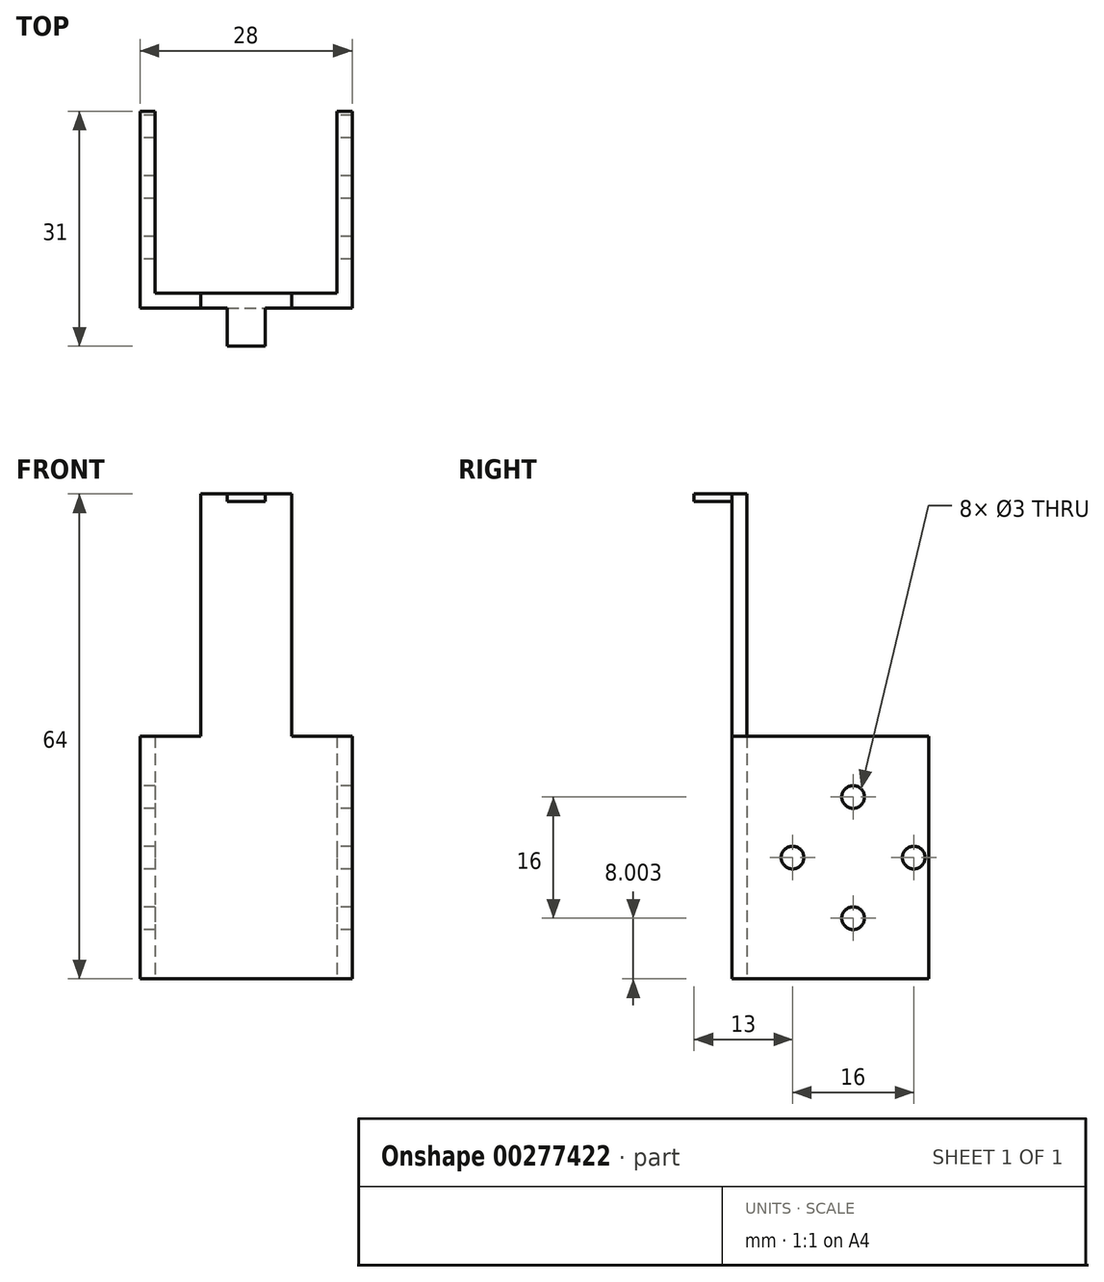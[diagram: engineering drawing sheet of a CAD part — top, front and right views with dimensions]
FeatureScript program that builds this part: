
annotation { "Feature Type Name" : "Feature", "Feature Type Description" : "" }
export const myFeature = defineFeature(function(context is Context, id is Id, definition is map)
    precondition{}
    {
        {
            var Q0;
            Q0=qCreatedBy(makeId("Front.planeOp"),FACE);
            var sketch = newSketch(context, id + "F0", { "sketchPlane" : qUnion([Q0])});
            skLineSegment(sketch, "E0.bottom", {"start": v(-7.9, 38.8) * mm, "end": v(4.1, 38.8) * mm});
            skLineSegment(sketch, "E0.top", {"start": v(-7.9, -25.2) * mm, "end": v(4.1, -25.2) * mm});
            skLineSegment(sketch, "E0.left", {"start": v(-7.9, 38.8) * mm, "end": v(-7.9, -25.2) * mm});
            skLineSegment(sketch, "E0.right", {"start": v(4.1, 38.8) * mm, "end": v(4.1, -25.2) * mm});
            skSolve(sketch);
        }
        {
            var Q0;
            Q0 = qSketchRegion(id + "F0", true);
            extrude(context, id + "F1", {"entities" : qUnion([Q0]), "depth" : 2 * mm});
        }
        {
            var Q0;
            Q0=makeQuery(id+"F1.opExtrude","SWEPT_FACE",FACE,{"disambiguationData":[OSD([sQuery(id+"F0.wireOp",EDGE,"E0.right")])]});
            var sketch = newSketch(context, id + "F2", { "sketchPlane" : qUnion([Q0])});
            skLineSegment(sketch, "E1", {"start": v(-2, 6.8) * mm, "end": v(0, 6.8) * mm});
            skSolve(sketch);
        }
        {
            var Q0;
            Q0 = qSketchRegion(id + "F2", true);
            var Q1;
            {var subQ0=sQuery(id+"F2.wireOp",EDGE,"E1");Q1=makeQuery(id+"F2.imprint","IMPRINT",FACE,{"disambiguationData":[TD([[makeQuery(id+"F2.imprint","IMPRINT",EDGE,{"derivedFrom":subQ0}),-1.0]])]});}
            extrude(context, id + "F3", {"entities" : qUnion([Q0, Q1]), "operationType" : NewBodyOperationType.ADD, "depth" : 8 * mm});
        }
        {
            var Q0;
            Q0=makeQuery(id+"F1.opExtrude","SWEPT_FACE",FACE,{"disambiguationData":[OSD([sQuery(id+"F0.wireOp",EDGE,"E0.left")])]});
            var sketch = newSketch(context, id + "F4", { "sketchPlane" : qUnion([Q0])});
            skLineSegment(sketch, "E2", {"start": v(2, 6.8) * mm, "end": v(0, 6.8) * mm});
            skSolve(sketch);
        }
        {
            var Q0;
            {var subQ0=sQuery(id+"F4.wireOp",EDGE,"E2");Q0=makeQuery(id+"F4.imprint","IMPRINT",FACE,{"disambiguationData":[TD([[makeQuery(id+"F4.imprint","IMPRINT",EDGE,{"derivedFrom":subQ0}),1.0]])]});}
            extrude(context, id + "F5", {"entities" : qUnion([Q0]), "operationType" : NewBodyOperationType.ADD, "depth" : 8 * mm});
        }
        {
            var Q0;
            {var subQ0=sQuery(id+"F0.wireOp",EDGE,"E0.left");var subQ1=makeQuery(id+"F1.opExtrude","CAP_EDGE",EDGE,{"disambiguationData":[OSD([subQ0])],"isStart":false});var subQ2=sQuery(id+"F0.wireOp",EDGE,"E0.top");var subQ3=sQuery(id+"F0.wireOp",EDGE,"E0.right");var subQ4=makeQuery(id+"F1.opExtrude","CAP_EDGE",EDGE,{"disambiguationData":[OSD([subQ3])],"isStart":false});Q0=makeQuery(id+"F5.boolean.opBoolean","MERGE",FACE,{"derivedFrom":[makeQuery(id+"F3.boolean.opBoolean","MERGE",FACE,{"derivedFrom":[makeQuery(id+"F1.opExtrude","CAP_FACE",FACE,{"disambiguationData":[OSD([sQuery(id+"F0.wireOp",EDGE,"E0.bottom"),subQ2,subQ0,subQ3])],"isStart":false}),makeQuery(id+"F3.opExtrude","SWEPT_FACE",FACE,{"disambiguationData":[OSD([subQ3]),TDD([makeQuery(id+"F2.imprint","IMPRINT",EDGE,{"disambiguationData":[TD([[makeQuery(id+"F2.imprint","INTERSECT",VERTEX,{"derivedFrom":[subQ4,sQuery(id+"F2.wireOp",EDGE,"E1")]}),-1.0]])],"derivedFrom":subQ4})])]})]}),makeQuery(id+"F5.opExtrude","SWEPT_FACE",FACE,{"disambiguationData":[OSD([subQ0]),TDD([makeQuery(id+"F4.imprint","IMPRINT",EDGE,{"disambiguationData":[TD([[makeQuery(id+"F4.imprint","INTERSECT",VERTEX,{"derivedFrom":[subQ1,sQuery(id+"F4.wireOp",EDGE,"E2")]}),-1.0]])],"derivedFrom":subQ1})])]})]});}
            var sketch = newSketch(context, id + "F6", { "sketchPlane" : qUnion([Q0])});
            skLineSegment(sketch, "E3.bottom", {"start": v(-4.4, 37.8) * mm, "end": v(0.6, 37.8) * mm});
            skLineSegment(sketch, "E3.top", {"start": v(-4.4, 39.8) * mm, "end": v(0.6, 39.8) * mm});
            skLineSegment(sketch, "E3.left", {"start": v(-4.4, 37.8) * mm, "end": v(-4.4, 39.8) * mm});
            skLineSegment(sketch, "E3.right", {"start": v(0.6, 37.8) * mm, "end": v(0.6, 39.8) * mm});
            skPoint(sketch, "E3.middle", {"position": v(-1.9, 38.8) * mm});
            skSolve(sketch);
        }
        {
            var Q0;
            Q0 = qSketchRegion(id + "F6", true);
            extrude(context, id + "F7", {"entities" : qUnion([Q0]), "operationType" : NewBodyOperationType.ADD, "depth" : 5 * mm});
        }
        {
            var Q0;
            Q0=makeQuery(id+"F7.opExtrude","SWEPT_FACE",FACE,{"disambiguationData":[OSD([sQuery(id+"F6.wireOp",EDGE,"E3.left")])]});
            var sketch = newSketch(context, id + "F8", { "sketchPlane" : qUnion([Q0])});
            skLineSegment(sketch, "E4", {"start": v(2, 38.8) * mm, "end": v(7, 38.8) * mm});
            skSolve(sketch);
        }
        {
            var Q0;
            Q0 = qSketchRegion(id + "F8", true);
            var Q1;
            {var subQ0=sQuery(id+"F8.wireOp",EDGE,"E4");Q1=makeQuery(id+"F8.imprint","IMPRINT",FACE,{"disambiguationData":[TD([[makeQuery(id+"F8.imprint","IMPRINT",EDGE,{"derivedFrom":subQ0}),1.0]])]});}
            extrude(context, id + "F9", {"entities" : qUnion([Q0, Q1]), "operationType" : NewBodyOperationType.REMOVE, "endBound" : BoundingType.THROUGH_ALL, "oppositeDirection" : true, "depth" : 25 * mm});
        }
        {
            var Q0;
            {var subQ0=sQuery(id+"F0.wireOp",EDGE,"E0.left");var subQ1=makeQuery(id+"F1.opExtrude","CAP_EDGE",EDGE,{"disambiguationData":[OSD([subQ0])],"isStart":true});var subQ2=sQuery(id+"F0.wireOp",EDGE,"E0.top");var subQ3=sQuery(id+"F0.wireOp",EDGE,"E0.right");var subQ4=makeQuery(id+"F1.opExtrude","CAP_EDGE",EDGE,{"disambiguationData":[OSD([subQ3])],"isStart":true});Q0=makeQuery(id+"F5.boolean.opBoolean","MERGE",FACE,{"derivedFrom":[makeQuery(id+"F3.boolean.opBoolean","MERGE",FACE,{"derivedFrom":[makeQuery(id+"F1.opExtrude","CAP_FACE",FACE,{"disambiguationData":[OSD([sQuery(id+"F0.wireOp",EDGE,"E0.bottom"),subQ2,subQ0,subQ3])],"isStart":true}),makeQuery(id+"F3.opExtrude","SWEPT_FACE",FACE,{"disambiguationData":[OSD([subQ3]),TDD([makeQuery(id+"F2.imprint","IMPRINT",EDGE,{"disambiguationData":[TD([[makeQuery(id+"F2.imprint","INTERSECT",VERTEX,{"derivedFrom":[subQ4,sQuery(id+"F2.wireOp",EDGE,"E1")]}),-1.0]])],"derivedFrom":subQ4})])]})]}),makeQuery(id+"F5.opExtrude","SWEPT_FACE",FACE,{"disambiguationData":[OSD([subQ0]),TDD([makeQuery(id+"F4.imprint","IMPRINT",EDGE,{"disambiguationData":[TD([[makeQuery(id+"F4.imprint","INTERSECT",VERTEX,{"derivedFrom":[subQ1,sQuery(id+"F4.wireOp",EDGE,"E2")]}),-1.0]])],"derivedFrom":subQ1})])]})]});}
            var sketch = newSketch(context, id + "F10", { "sketchPlane" : qUnion([Q0])});
            skLineSegment(sketch, "E5.bottom", {"start": v(13.9, 6.8) * mm, "end": v(15.9, 6.8) * mm});
            skLineSegment(sketch, "E5.top", {"start": v(13.9, -25.2) * mm, "end": v(15.9, -25.2) * mm});
            skLineSegment(sketch, "E5.left", {"start": v(13.9, 6.8) * mm, "end": v(13.9, -25.2) * mm});
            skLineSegment(sketch, "E5.right", {"start": v(15.9, 6.8) * mm, "end": v(15.9, -25.2) * mm});
            skLineSegment(sketch, "E6.bottom", {"start": v(-12.1, 6.8) * mm, "end": v(-10.1, 6.8) * mm});
            skLineSegment(sketch, "E6.top", {"start": v(-12.1, -25.2) * mm, "end": v(-10.1, -25.2) * mm});
            skLineSegment(sketch, "E6.left", {"start": v(-12.1, 6.8) * mm, "end": v(-12.1, -25.2) * mm});
            skLineSegment(sketch, "E6.right", {"start": v(-10.1, 6.8) * mm, "end": v(-10.1, -25.2) * mm});
            skSolve(sketch);
        }
        {
            var Q0;
            Q0=makeQuery(id+"F10.imprint","IMPRINT",FACE,{"disambiguationData":[TD([[makeQuery(id+"F10.imprint","IMPRINT",EDGE,{"derivedFrom":sQuery(id+"F10.wireOp",EDGE,"E6.bottom")}),-1.0]])]});
            var Q1;
            Q1=makeQuery(id+"F10.imprint","IMPRINT",FACE,{"disambiguationData":[TD([[makeQuery(id+"F10.imprint","IMPRINT",EDGE,{"derivedFrom":sQuery(id+"F10.wireOp",EDGE,"E5.bottom")}),1.0]])]});
            extrude(context, id + "F11", {"entities" : qUnion([Q0, Q1]), "operationType" : NewBodyOperationType.ADD, "depth" : 24 * mm});
        }
        {
            var Q0;
            Q0=makeQuery(id+"F11.boolean.opBoolean","MERGE",FACE,{"derivedFrom":[makeQuery(id+"F5.opExtrude","CAP_FACE",FACE,{"disambiguationData":[OSD([sQuery(id+"F0.wireOp",EDGE,"E0.top"),sQuery(id+"F0.wireOp",EDGE,"E0.left"),sQuery(id+"F4.wireOp",EDGE,"E2")])],"isStart":false}),makeQuery(id+"F11.opExtrude","SWEPT_FACE",FACE,{"disambiguationData":[OSD([sQuery(id+"F10.wireOp",EDGE,"E5.right")])]})]});
            var sketch = newSketch(context, id + "F12", { "sketchPlane" : qUnion([Q0])});
            skLineSegment(sketch, "E7", {"start": v(-11, 6.8) * mm, "end": v(-11, -25.2) * mm});
            skLineSegment(sketch, "E8", {"start": v(-24, -9.2) * mm, "end": v(2, -9.2) * mm});
            skCircle(sketch, "E9", {"center": v(-6, -9.2) * mm, "radius": 1.5 * mm});
            skLineSegment(sketch, "E10", {"start": v(2, -9.2) * mm, "end": v(-14, -9.2) * mm});
            skCircle(sketch, "E11.1.0", {"center": v(-14, -1.2) * mm, "radius": 1.5 * mm});
            skCircle(sketch, "E11.2.0", {"center": v(-22, -9.2) * mm, "radius": 1.5 * mm});
            skCircle(sketch, "E11.3.0", {"center": v(-14, -17.2) * mm, "radius": 1.5 * mm});
            skPoint(sketch, "E11.center", {"position": v(-14, -9.2) * mm});
            skSolve(sketch);
        }
        {
            var Q0;
            Q0=makeQuery(id+"F12.imprint","IMPRINT",FACE,{"disambiguationData":[TD([[makeQuery(id+"F12.imprint","IMPRINT",EDGE,{"derivedFrom":sQuery(id+"F12.wireOp",EDGE,"E11.1.0")}),1.0]])]});
            var Q1;
            Q1=makeQuery(id+"F12.imprint","IMPRINT",FACE,{"disambiguationData":[TD([[makeQuery(id+"F12.imprint","IMPRINT",EDGE,{"derivedFrom":sQuery(id+"F12.wireOp",EDGE,"E11.3.0")}),1.0]])]});
            var Q2;
            {var subQ0=sQuery(id+"F12.wireOp",EDGE,"E11.2.0");var subQ1=sQuery(id+"F12.wireOp",EDGE,"E8");var subQ2=makeQuery(id+"F12.imprint","INTERSECT",VERTEX,{"disambiguationData":[OD(0.0)],"derivedFrom":[subQ1,subQ0]});Q2=makeQuery(id+"F12.imprint","IMPRINT",FACE,{"disambiguationData":[TD([[makeQuery(id+"F12.imprint","IMPRINT",EDGE,{"disambiguationData":[TD([[subQ2,-1.0]])],"derivedFrom":subQ1}),1.0]])]});}
            var Q3;
            {var subQ0=sQuery(id+"F12.wireOp",EDGE,"E10");var subQ1=sQuery(id+"F12.wireOp",EDGE,"E9");var subQ2=makeQuery(id+"F12.imprint","INTERSECT",VERTEX,{"disambiguationData":[OD(0.0)],"derivedFrom":[subQ1,subQ0]});Q3=makeQuery(id+"F12.imprint","IMPRINT",FACE,{"disambiguationData":[TD([[makeQuery(id+"F12.imprint","IMPRINT",EDGE,{"disambiguationData":[TD([[subQ2,-1.0]])],"derivedFrom":subQ1}),1.0]])]});}
            var Q4;
            {var subQ0=sQuery(id+"F12.wireOp",EDGE,"E10");var subQ1=sQuery(id+"F12.wireOp",EDGE,"E9");var subQ2=makeQuery(id+"F12.imprint","INTERSECT",VERTEX,{"disambiguationData":[OD(0.0)],"derivedFrom":[subQ1,subQ0]});Q4=makeQuery(id+"F12.imprint","IMPRINT",FACE,{"disambiguationData":[TD([[makeQuery(id+"F12.imprint","IMPRINT",EDGE,{"disambiguationData":[TD([[subQ2,1.0]])],"derivedFrom":subQ1}),1.0]])]});}
            var Q5;
            {var subQ0=sQuery(id+"F12.wireOp",EDGE,"E11.2.0");var subQ1=sQuery(id+"F12.wireOp",EDGE,"E8");var subQ2=makeQuery(id+"F12.imprint","INTERSECT",VERTEX,{"disambiguationData":[OD(0.0)],"derivedFrom":[subQ1,subQ0]});Q5=makeQuery(id+"F12.imprint","IMPRINT",FACE,{"disambiguationData":[TD([[makeQuery(id+"F12.imprint","IMPRINT",EDGE,{"disambiguationData":[TD([[subQ2,-1.0]])],"derivedFrom":subQ1}),-1.0]])]});}
            extrude(context, id + "F13", {"entities" : qUnion([Q0, Q1, Q2, Q3, Q4, Q5]), "operationType" : NewBodyOperationType.REMOVE, "endBound" : BoundingType.THROUGH_ALL, "oppositeDirection" : true, "depth" : 25 * mm});
        }
    });
